# Revit family: ECWP710J-H
name_source: partatom
category: HLS-Bauteile
revit_build: Autodesk Revit 2016 (Build: 20150714_1515(x64)
units: mm (PartAtom-declared; Revit-internal decimal feet)

## family parameters
Arbeitsebenenbasiert = Nein
Beim Laden mit Abzugskörper schneiden = Nein
Bemaßung runder Anschluss = Durchmesser verwenden
Gemeinsam genutzt = Nein
Immer vertikal = Ja
OmniClass-Nummer = 23.75.10.21
OmniClass-Titel = Heat Pumps
Raumberechnungspunkt = Nein
Teiletyp = Normal

## types (1)
- ECWP710J-H
    ALG_Gasversorgungsdruck_in_mbar = 17-25
    ALG_Gewicht_in_kg = 1080
    ALG_ManufacturerCode = ECWP710J-H
    ALG_Max_Gasaufnahme_in_kW = 79
    ALG_Schalldruckpegel_Leiselauf_in_dB(A) = 59
    ALG_Schalldruckpegel_Max_in_dB(A) = 66
    ALG_Schalldruckpegel_Nominal_in_dB(A) = 62
    ALG_Ventilator_Externe_Pressung_in_Pa = 5 (30 über Software)
    ALG_Ventilator_Luftmege_in_m3/h = 34200
    Beschreibung = Gasmotorwärmepumpe (Kompaktmaschine/Chiller)
    HLS_Bezeichnung_2 = ECWP710J-H
    HLS_Breite = 800 mm
    HLS_Höhe = 2170 mm
    HLS_Länge = 2100 mm
    HLS_Typ = ECWP710J-H
    Hersteller = YANMAR
    Modell = ECWP710J-H
    Nenndruckverlust (Heizen) in kPa = 24
    Nennleistung (Heizen) in kW = 81,5
    Nennleistung (Kühlen) in kW = 71,0
    Nennvolumenstrom (Heizen) in m3/h = 12.2
    Typenkommentare = Gasmotorwärmepumpe (Kompaktmaschine/Chiller)
    URL = www.energysystem-yanmar.de

## geometry (parser evidence)
native form markers: Blend x9
no freeform markers — native parametric forms only
